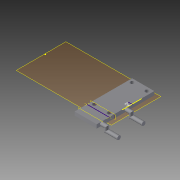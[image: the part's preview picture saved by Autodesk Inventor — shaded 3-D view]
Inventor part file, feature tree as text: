
AUTODESK INVENTOR PART (.ipt)
format: ipt  version: 2015 (Build 190159000, 159)  size: 329,216 bytes
history: native  units: in
note: dims shown in document units (in); Inventor stores cm internally (conversion verified against a paired STEP export)
features: sketch x27, extrude x22, plane x5, fillet x2, mirror x2, pattern_circular x1, sweep x1
ambient origin geometry x8: Origin, YZ Plane, XZ Plane, XY Plane, X Axis, Y Axis, Z Axis, Center Point
bodies: Solid1 (feature_tree)
feature tree (60):
  extrude  "Extrusion1"  Depth=0.1181in
  fillet  "Fillet1"  Radius=0.1969in
  fillet  "Fillet2"  [1 undecoded]
  plane  "Work Plane1"
  extrude  "Extrusion3"  Depth=0.1181in
  pattern_circular  "Circular Pattern1"  Count=4 Angle=360.0deg
  extrude  "Extrusion5"  Depth=0.1181in TaperAngle=0.0deg
  extrude  "Extrusion6"  Depth=0.1181in TaperAngle=0.0deg
  extrude  "Extrusion7"  Depth=0.3937in TaperAngle=0.0deg
  sketch  "Sketch11"  dims[d39=0.1969in d40=0.1181in d41=0.0in]
  extrude  "Extrusion8"  Depth=3.937in TaperAngle=0.0deg
  extrude  "Extrusion9"  Depth=0.1181in TaperAngle=0.0deg
  extrude  "Extrusion10"  Depth=0.5512in
  extrude  "Extrusion11"  Depth=0.7087in
  extrude  "Extrusion12"  Depth=0.3937in
  extrude  "Extrusion13"  Depth=0.1181in TaperAngle=0.0deg
  extrude  "Extrusion14"  Depth=0.0106in TaperAngle=0.0deg
  extrude  "Extrusion16"  Depth=0.1181in TaperAngle=0.0deg
  extrude  "Extrusion17"  Depth=0.2953in
  extrude  "Extrusion18"  Depth=0.1181in
  extrude  "Extrusion19"  Depth=0.1181in
  extrude  "Extrusion21"  Depth=0.1181in
  extrude  "Extrusion22"  Depth=0.2953in TaperAngle=0.0deg
  extrude  "Extrusion23"  TaperAngle=0.0deg  [1 undecoded]
  extrude  "Extrusion24"  Depth=0.3937in TaperAngle=0.0deg
  mirror  "Mirror1"
  sketch  "Sketch36"  dims[d100=1.1811in d101=0.0in d102=0.3937in d103=0.0in]
  sketch  "Sketch37"  dims[d104=0.3543in d105=0.1575in]
  plane  "Work Plane2"
  extrude  "Extrusion25"  Depth=0.1575in
  extrude  "Extrusion26"  Depth=0.1575in
  sketch  "Sketch40"  dims[d110=0.0in d111=0.0in]
  plane  "Work Plane3"
  sweep  "Sweep1"
  plane  "Work Plane4"
  mirror  "Mirror2"
  sketch  "Sketch1"  dims[d4=0.1181in d5=0.0in d6=0.1969in d7=0.1969in d8=-0.1969in]
  sketch  "Sketch6"  dims[d17=0.7087in d21=0.1181in]
  sketch  "Sketch8"  dims[d22=0.1181in]
  sketch  "Sketch9"  dims[d24=0.7087in d25=0.0in d26=1.5748in d27=360.0deg]
  sketch  "Sketch10"  dims[d35=0.1969in d36=0.1181in d37=0.0in]
  sketch  "Sketch12"  dims[d42=0.3937in d43=0.0in d44=3.937in d45=0.0in]
  sketch  "Sketch13"  dims[d46=3.937in d47=0.0in d48=3.937in d49=0.0in]
  sketch  "Sketch14"  dims[d50=0.1181in d51=3.937in d52=0.0in]
  sketch  "Sketch17"  dims[d53=0.5118in d54=0.0in d55=0.5512in]
  sketch  "Sketch18"  dims[d56=0.126in d57=0.7087in]
  sketch  "Sketch20"  dims[d58=0.3937in d59=0.3937in]
  sketch  "Sketch22"  dims[d60=0.7087in d61=0.0in d62=0.1181in d63=0.0in]
  sketch  "Sketch24"  dims[d69=0.0118in d70=0.0in d71=0.0106in d72=0.0in]
  sketch  "Sketch25"  dims[d73=0.0012in d74=0.0in d75=0.1181in d76=0.0in]
  sketch  "Sketch26"  dims[d84=1.1811in d85=0.0in d86=0.2953in]
  sketch  "Sketch27"  dims[d87=0.7087in d88=0.0in d89=0.1181in]
  sketch  "Sketch32"  dims[d90=0.1181in d91=0.1181in]
  sketch  "Sketch33"  dims[d92=0.1181in d93=0.1181in]
  sketch  "Sketch34"  dims[d94=0.7087in d95=0.0in d96=0.2953in d97=0.0in]
  sketch  "Sketch35"  dims[d98=0.1181in d99=0.0in]
  sketch  "Sketch38"  dims[d106=-0.1575in d107=0.1575in]
  sketch  "Sketch39"  dims[d108=0.1181in d109=0.3937in]
  sketch  "Sketch41"  dims[d112=-0.5512in]
  plane  "Work Plane5"
note: 2 required parameter values undecoded (feature->parameter linkage not recoverable at this tier; creation-order binding heuristic only, values carry confidence <= 0.55)
